# Revit family: HermanMiller_Seating_KNN4_KeynChair4-LegBase
name_source: partatom
category: Furniture
revit_build: Autodesk Revit Architecture 2014 (Build: 20130308_1515(x64)
units: mm (PartAtom-declared; Revit-internal decimal feet)

## types (4) — shared parameters
Assembly Code = E2020200
Manufacturer = Herman Miller, Inc.
Package Qty = 1
URL = http://www.hermanmiller.com

## per-type parameters (varying)
| type | Armless | Arms | Casters | Chair Type | Description | Fxd Arms Casters | Fxd Arms Glides | Model | No Arms Casters | No Arms Glides |
| Seat Pad No Arms Glides | Yes | No | No | 1 | Keyn Chair 4-Leg Base Seat Pad No Arms | No | No | KNN4SN | No | Yes |
| Seat Pad Fxd Arms Glides | No | Yes | No | 2 | Keyn Chair 4-Leg Base Seat Pad Fixed Arms | No | Yes | KNN4SP | No | No |
| Seat Pad No Arms Casters | Yes | No | Yes | 3 | Keyn Chair 4-Leg Base Seat Pad No Arms | No | No | KNN4SN | Yes | No |
| Seat Pad Fxd Arms Casters | No | Yes | Yes | 4 | Keyn Chair 4-Leg Base Seat Pad Fixed Arms | Yes | No | KNN4SP | No | No |

## geometry (parser evidence)
native form markers: Sweep x2
no freeform markers — native parametric forms only
